# Revit family: PF 45
name_source: partatom
category: Attrezzature speciali
revit_build: Autodesk Revit 2016 (Build: 20150714_1515(x64)
units: mm (PartAtom-declared; Revit-internal decimal feet)

## family parameters
Basato su piano di lavoro = No
Condiviso = No
Punto di calcolo locali = No
Quota connettore circolare = Usa diametro
Sempre verticale = Sì
Taglio con vuoti quando caricato = No
Tipo di parte = Normale

## types (3) — shared parameters
230 Volt = No
400 Volt = Sì
Apparent power = 43600 VA
Capacity factor = 0.80%
Clearance = 400 mm  [stored 1.31234 ft]
Electrical supply = 400 V
Height = 825 mm
Installed Load = 5.5 kW
Latent Heat = 0.44 kW
Length = 605 mm
Output racks/h = 40
Overall size = 1020 mm
Rack size = 500 x 500
Rinse water consumption = 2.5 L
Sensible Heat = 1.14 kW
Tank drain = 35 mm  [stored 0.114829 ft]
Total absorption = 11 A
Water inlet = 1"
Width = 600 mm

## per-type parameters (varying)
| type | Air gap | Water softener |
| PF 45 | No | No |
| PF 45 R | Sì | No |
| PF 45 RA | Sì | Sì |

note: [stored X ft] marks values corroborated as IEEE doubles in the binary element streams (Revit-internal decimal feet)
